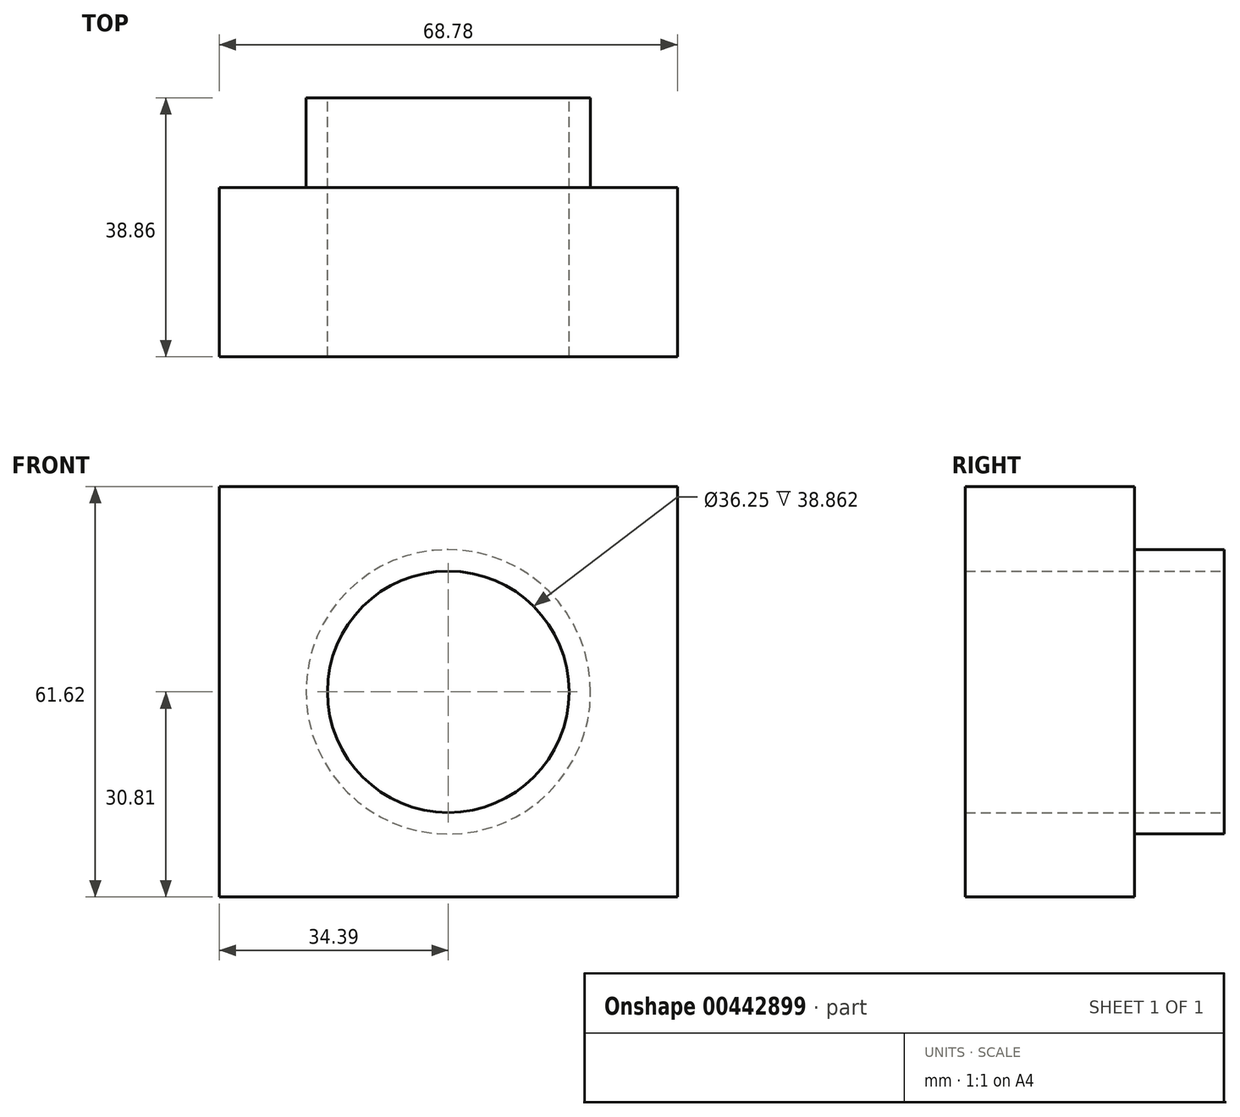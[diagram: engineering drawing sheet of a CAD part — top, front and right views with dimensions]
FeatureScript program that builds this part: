
annotation { "Feature Type Name" : "Feature", "Feature Type Description" : "" }
export const myFeature = defineFeature(function(context is Context, id is Id, definition is map)
    precondition{}
    {
        {
            var Q0;
            Q0=qCreatedBy(makeId("Front.planeOp"),FACE);
            var sketch = newSketch(context, id + "F0", { "sketchPlane" : qUnion([Q0])});
            skLineSegment(sketch, "E0.bottom", {"start": v(-34.39, 30.8) * mm, "end": v(34.39, 30.8) * mm});
            skLineSegment(sketch, "E0.top", {"start": v(-34.39, -30.8) * mm, "end": v(34.39, -30.8) * mm});
            skLineSegment(sketch, "E0.left", {"start": v(-34.39, 30.8) * mm, "end": v(-34.39, -30.8) * mm});
            skLineSegment(sketch, "E0.right", {"start": v(34.39, 30.8) * mm, "end": v(34.39, -30.8) * mm});
            skPoint(sketch, "E0.middle", {"position": v(0, 0) * mm});
            skSolve(sketch);
        }
        {
            var Q0;
            Q0=makeQuery(id+"F0.imprint","IMPRINT",FACE,{"disambiguationData":[TD([[makeQuery(id+"F0.imprint","IMPRINT",EDGE,{"derivedFrom":sQuery(id+"F0.wireOp",EDGE,"E0.bottom")}),-1.0]])]});
            extrude(context, id + "F1", {"entities" : qUnion([Q0]), "depth" : 25.4 * mm});
        }
        {
            var Q0;
            Q0=makeQuery(id+"F0.imprint","IMPRINT",FACE,{"disambiguationData":[TD([[makeQuery(id+"F0.imprint","IMPRINT",EDGE,{"derivedFrom":sQuery(id+"F0.wireOp",EDGE,"E0.bottom")}),-1.0]])]});
            var sketch = newSketch(context, id + "F2", { "sketchPlane" : qUnion([Q0])});
            skCircle(sketch, "E1", {"center": v(0, 0) * mm, "radius": 21.35 * mm});
            skSolve(sketch);
        }
        {
            var Q0;
            Q0 = qSketchRegion(id + "F2", true);
            extrude(context, id + "F3", {"entities" : qUnion([Q0]), "operationType" : NewBodyOperationType.ADD, "oppositeDirection" : true, "depth" : 13.46 * mm});
        }
        {
            var Q0;
            Q0=makeQuery(id+"F3.opExtrude","CAP_FACE",FACE,{"disambiguationData":[OSD([sQuery(id+"F2.wireOp",EDGE,"E1")])],"isStart":false});
            var sketch = newSketch(context, id + "F4", { "sketchPlane" : qUnion([Q0])});
            skCircle(sketch, "E2", {"center": v(0, 0) * mm, "radius": 18.13 * mm});
            skSolve(sketch);
        }
        {
            var Q0;
            Q0=makeQuery(id+"F4.imprint","IMPRINT",FACE,{"disambiguationData":[TD([[makeQuery(id+"F4.imprint","IMPRINT",EDGE,{"derivedFrom":sQuery(id+"F4.wireOp",EDGE,"E2")}),1.0]])]});
            extrude(context, id + "F5", {"entities" : qUnion([Q0]), "operationType" : NewBodyOperationType.REMOVE, "oppositeDirection" : true, "depth" : 60.45 * mm});
        }
    });
